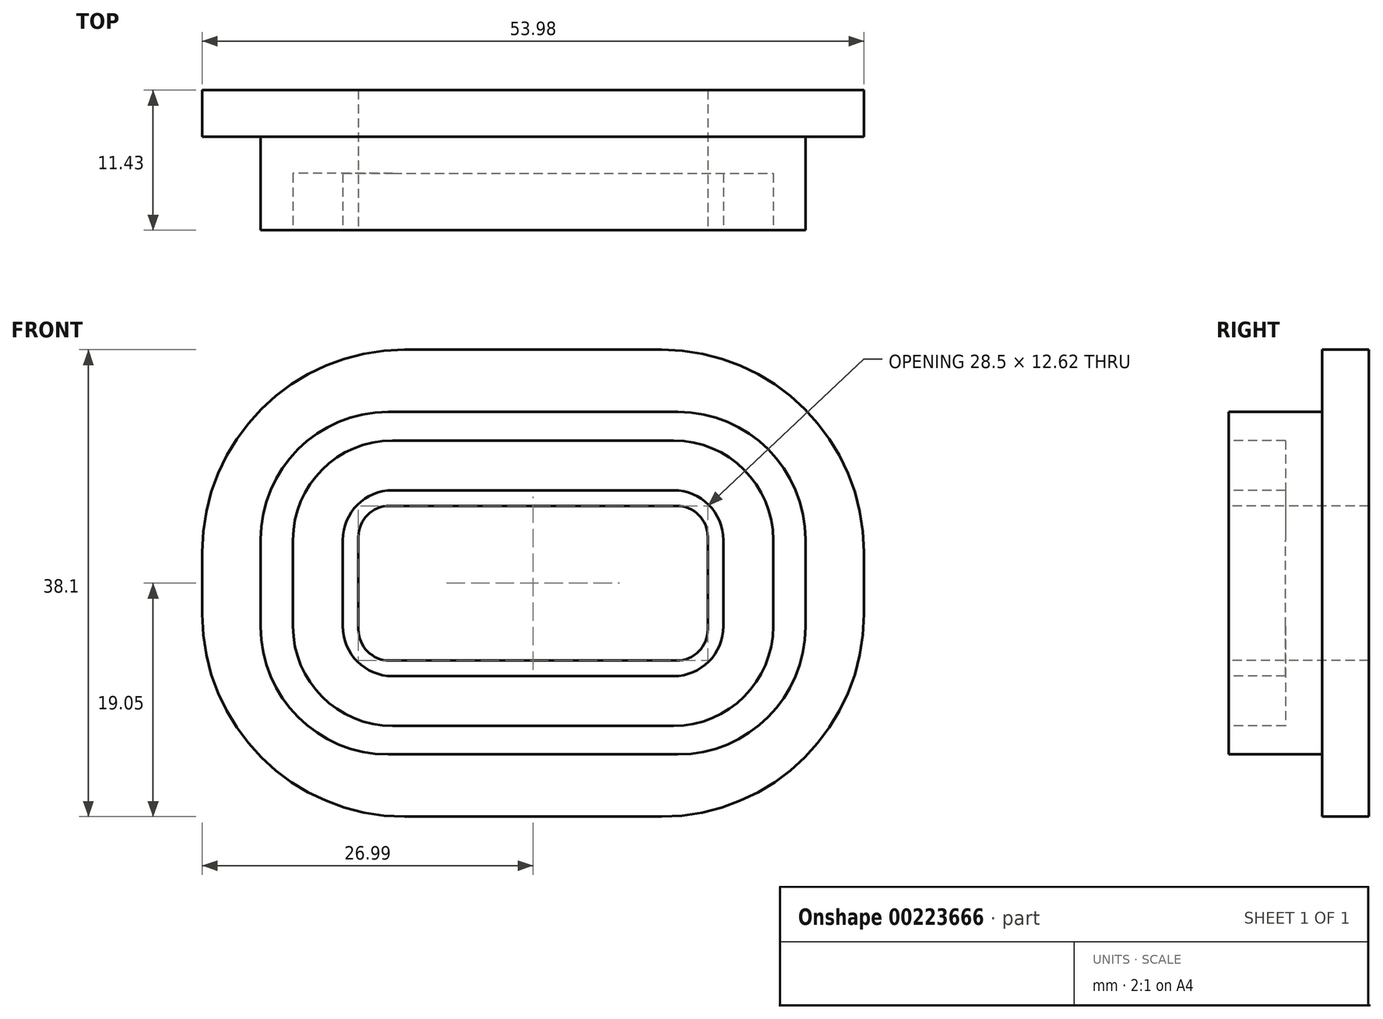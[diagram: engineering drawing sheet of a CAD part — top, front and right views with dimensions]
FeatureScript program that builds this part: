
annotation { "Feature Type Name" : "Feature", "Feature Type Description" : "" }
export const myFeature = defineFeature(function(context is Context, id is Id, definition is map)
    precondition{}
    {
        {
            var Q0;
            Q0=qCreatedBy(makeId("Front.planeOp"),FACE);
            var sketch = newSketch(context, id + "F0", { "sketchPlane" : qUnion([Q0])});
            skLineSegment(sketch, "E0.bottom", {"start": v(-10.48, -19.05) * mm, "end": v(10.48, -19.05) * mm});
            skLineSegment(sketch, "E0.top", {"start": v(-10.48, 19.05) * mm, "end": v(10.48, 19.05) * mm});
            skLineSegment(sketch, "E0.left", {"start": v(-26.99, -2.54) * mm, "end": v(-26.99, 2.54) * mm});
            skLineSegment(sketch, "E0.right", {"start": v(26.99, -2.54) * mm, "end": v(26.99, 2.54) * mm});
            skPoint(sketch, "E0.middle", {"position": v(0, 0) * mm});
            skPoint(sketch, "E1.visualSharp", {"position": v(-26.99, 19.05) * mm});
            skArc(sketch, "E1.filletArc", {"start": v(-10.48, 19.05) * mm, "mid": v(-22.15, 14.21) * mm, "end": v(-26.99, 2.54) * mm});
            skPoint(sketch, "E2.visualSharp", {"position": v(26.99, 19.05) * mm});
            skArc(sketch, "E2.filletArc", {"start": v(26.99, 2.54) * mm, "mid": v(22.15, 14.21) * mm, "end": v(10.48, 19.05) * mm});
            skPoint(sketch, "E3.visualSharp", {"position": v(26.99, -19.05) * mm});
            skArc(sketch, "E3.filletArc", {"start": v(10.48, -19.05) * mm, "mid": v(22.15, -14.21) * mm, "end": v(26.99, -2.54) * mm});
            skPoint(sketch, "E4.visualSharp", {"position": v(-26.99, -19.05) * mm});
            skArc(sketch, "E4.filletArc", {"start": v(-26.99, -2.54) * mm, "mid": v(-22.15, -14.21) * mm, "end": v(-10.48, -19.05) * mm});
            skSolve(sketch);
        }
        {
            var Q0;
            Q0 = qSketchRegion(id + "F0", true);
            var Q1;
            Q1 = qConstructionFilter(qBodyType(qCreatedBy(id + "F0" ,EDGE), BodyType.WIRE), ConstructionObject.NO);
            extrude(context, id + "F1", {"entities" : qUnion([Q0]), "surfaceEntities" : qUnion([Q1]), "depth" : 3.8 * mm});
        }
        {
            var Q0;
            Q0=makeQuery(id+"F1.opExtrude","CAP_FACE",FACE,{"disambiguationData":[OSD([sQuery(id+"F0.wireOp",EDGE,"E0.bottom"),sQuery(id+"F0.wireOp",EDGE,"E0.top"),sQuery(id+"F0.wireOp",EDGE,"E0.left"),sQuery(id+"F0.wireOp",EDGE,"E0.right")])],"isStart":false});
            var sketch = newSketch(context, id + "F2", { "sketchPlane" : qUnion([Q0])});
            skLineSegment(sketch, "E5.bottom", {"start": v(-11.81, -13.97) * mm, "end": v(11.81, -13.97) * mm});
            skLineSegment(sketch, "E5.top", {"start": v(-11.81, 13.97) * mm, "end": v(11.81, 13.97) * mm});
            skLineSegment(sketch, "E5.left", {"start": v(-22.23, -3.56) * mm, "end": v(-22.23, 3.56) * mm});
            skLineSegment(sketch, "E5.right", {"start": v(22.23, -3.56) * mm, "end": v(22.23, 3.56) * mm});
            skPoint(sketch, "E5.middle", {"position": v(0, 0) * mm});
            skPoint(sketch, "E6.visualSharp", {"position": v(-22.23, 13.97) * mm});
            skArc(sketch, "E6.filletArc", {"start": v(-11.81, 13.97) * mm, "mid": v(-19.17, 10.92) * mm, "end": v(-22.23, 3.56) * mm});
            skPoint(sketch, "E7.visualSharp", {"position": v(22.23, 13.97) * mm});
            skArc(sketch, "E7.filletArc", {"start": v(22.23, 3.56) * mm, "mid": v(19.17, 10.92) * mm, "end": v(11.81, 13.97) * mm});
            skPoint(sketch, "E8.visualSharp", {"position": v(22.23, -13.97) * mm});
            skArc(sketch, "E8.filletArc", {"start": v(11.81, -13.97) * mm, "mid": v(19.17, -10.92) * mm, "end": v(22.23, -3.56) * mm});
            skPoint(sketch, "E9.visualSharp", {"position": v(-22.22, -13.97) * mm});
            skArc(sketch, "E9.filletArc", {"start": v(-22.23, -3.56) * mm, "mid": v(-19.17, -10.92) * mm, "end": v(-11.81, -13.97) * mm});
            skSolve(sketch);
        }
        {
            var Q0;
            Q0 = qSketchRegion(id + "F2", true);
            extrude(context, id + "F3", {"entities" : qUnion([Q0]), "operationType" : NewBodyOperationType.ADD, "depth" : 7.62 * mm});
        }
        {
            var Q0;
            Q0=makeQuery(id+"F3.opExtrude","CAP_FACE",FACE,{"disambiguationData":[OSD([sQuery(id+"F2.wireOp",EDGE,"E5.bottom"),sQuery(id+"F2.wireOp",EDGE,"E5.top"),sQuery(id+"F2.wireOp",EDGE,"E5.left"),sQuery(id+"F2.wireOp",EDGE,"E5.right"),sQuery(id+"F2.wireOp",EDGE,"E6.filletArc"),sQuery(id+"F2.wireOp",EDGE,"E7.filletArc"),sQuery(id+"F2.wireOp",EDGE,"E8.filletArc"),sQuery(id+"F2.wireOp",EDGE,"E9.filletArc")])],"isStart":false});
            var sketch = newSketch(context, id + "F4", { "sketchPlane" : qUnion([Q0])});
            skLineSegment(sketch, "E10.bottom", {"start": v(-11.7, -6.31) * mm, "end": v(11.7, -6.31) * mm});
            skLineSegment(sketch, "E10.top", {"start": v(-11.7, 6.31) * mm, "end": v(11.7, 6.31) * mm});
            skLineSegment(sketch, "E10.left", {"start": v(-14.25, -3.77) * mm, "end": v(-14.25, 3.77) * mm});
            skLineSegment(sketch, "E10.right", {"start": v(14.25, -3.77) * mm, "end": v(14.25, 3.77) * mm});
            skPoint(sketch, "E10.middle", {"position": v(0, 0) * mm});
            skPoint(sketch, "E11.visualSharp", {"position": v(14.25, 6.31) * mm});
            skArc(sketch, "E11.filletArc", {"start": v(14.25, 3.77) * mm, "mid": v(13.5, 5.57) * mm, "end": v(11.7, 6.31) * mm});
            skPoint(sketch, "E12.visualSharp", {"position": v(14.25, -6.31) * mm});
            skArc(sketch, "E12.filletArc", {"start": v(11.7, -6.31) * mm, "mid": v(13.5, -5.57) * mm, "end": v(14.25, -3.77) * mm});
            skPoint(sketch, "E13.visualSharp", {"position": v(-14.25, -6.31) * mm});
            skArc(sketch, "E13.filletArc", {"start": v(-14.25, -3.77) * mm, "mid": v(-13.5, -5.57) * mm, "end": v(-11.7, -6.31) * mm});
            skPoint(sketch, "E14.visualSharp", {"position": v(-14.25, 6.31) * mm});
            skArc(sketch, "E14.filletArc", {"start": v(-11.7, 6.31) * mm, "mid": v(-13.5, 5.57) * mm, "end": v(-14.25, 3.77) * mm});
            skSolve(sketch);
        }
        {
            var Q0;
            Q0 = qSketchRegion(id + "F4", true);
            var Q1;
            Q1=makeQuery(id+"F4.imprint","IMPRINT",FACE,{"disambiguationData":[TD([[makeQuery(id+"F4.imprint","IMPRINT",EDGE,{"derivedFrom":sQuery(id+"F4.wireOp",EDGE,"E10.bottom")}),1.0]])]});
            extrude(context, id + "F5", {"entities" : qUnion([Q0, Q1]), "operationType" : NewBodyOperationType.REMOVE, "endBound" : BoundingType.THROUGH_ALL, "oppositeDirection" : true, "depth" : 25.4 * mm});
        }
        {
            var Q0;
            Q0=makeQuery(id+"F3.opExtrude","CAP_FACE",FACE,{"disambiguationData":[OSD([sQuery(id+"F2.wireOp",EDGE,"E5.bottom"),sQuery(id+"F2.wireOp",EDGE,"E5.top"),sQuery(id+"F2.wireOp",EDGE,"E5.left"),sQuery(id+"F2.wireOp",EDGE,"E5.right"),sQuery(id+"F2.wireOp",EDGE,"E6.filletArc"),sQuery(id+"F2.wireOp",EDGE,"E7.filletArc"),sQuery(id+"F2.wireOp",EDGE,"E8.filletArc"),sQuery(id+"F2.wireOp",EDGE,"E9.filletArc")])],"isStart":false});
            var sketch = newSketch(context, id + "F6", { "sketchPlane" : qUnion([Q0])});
            skLineSegment(sketch, "E15.bottom", {"start": v(-11.46, -7.58) * mm, "end": v(11.46, -7.58) * mm});
            skLineSegment(sketch, "E15.top", {"start": v(-11.46, 7.58) * mm, "end": v(11.46, 7.58) * mm});
            skLineSegment(sketch, "E15.left", {"start": v(-15.52, -3.52) * mm, "end": v(-15.52, 3.52) * mm});
            skLineSegment(sketch, "E15.right", {"start": v(15.52, -3.52) * mm, "end": v(15.52, 3.52) * mm});
            skPoint(sketch, "E15.middle", {"position": v(0, 0) * mm});
            skPoint(sketch, "E16.visualSharp", {"position": v(15.52, 7.58) * mm});
            skArc(sketch, "E16.filletArc", {"start": v(15.52, 3.52) * mm, "mid": v(14.33, 6.4) * mm, "end": v(11.46, 7.58) * mm});
            skPoint(sketch, "E17.visualSharp", {"position": v(15.52, -7.58) * mm});
            skArc(sketch, "E17.filletArc", {"start": v(11.46, -7.58) * mm, "mid": v(14.33, -6.4) * mm, "end": v(15.52, -3.52) * mm});
            skPoint(sketch, "E18.visualSharp", {"position": v(-15.52, -7.58) * mm});
            skArc(sketch, "E18.filletArc", {"start": v(-15.52, -3.52) * mm, "mid": v(-14.33, -6.4) * mm, "end": v(-11.46, -7.58) * mm});
            skPoint(sketch, "E19.visualSharp", {"position": v(-15.52, 7.58) * mm});
            skArc(sketch, "E19.filletArc", {"start": v(-11.46, 7.58) * mm, "mid": v(-14.33, 6.4) * mm, "end": v(-15.52, 3.52) * mm});
            skArc(sketch, "E20.0", {"start": v(-11.46, 11.65) * mm, "mid": v(-17.2, 9.27) * mm, "end": v(-19.58, 3.52) * mm});
            skLineSegment(sketch, "E20.1", {"start": v(-19.58, -3.52) * mm, "end": v(-19.58, 3.52) * mm});
            skLineSegment(sketch, "E20.2", {"start": v(-11.46, 11.65) * mm, "end": v(11.46, 11.65) * mm});
            skArc(sketch, "E20.3", {"start": v(-19.58, -3.52) * mm, "mid": v(-17.2, -9.27) * mm, "end": v(-11.46, -11.65) * mm});
            skArc(sketch, "E20.4", {"start": v(19.58, 3.52) * mm, "mid": v(17.2, 9.27) * mm, "end": v(11.46, 11.65) * mm});
            skLineSegment(sketch, "E20.5", {"start": v(19.58, -3.52) * mm, "end": v(19.58, 3.52) * mm});
            skArc(sketch, "E20.6", {"start": v(11.46, -11.65) * mm, "mid": v(17.2, -9.27) * mm, "end": v(19.58, -3.52) * mm});
            skLineSegment(sketch, "E20.7", {"start": v(-11.46, -11.65) * mm, "end": v(11.46, -11.65) * mm});
            skSolve(sketch);
        }
        {
            var Q0;
            Q0 = qSketchRegion(id + "F6", true);
            extrude(context, id + "F7", {"entities" : qUnion([Q0]), "operationType" : NewBodyOperationType.REMOVE, "oppositeDirection" : true, "depth" : 4.63 * mm});
        }
    });
